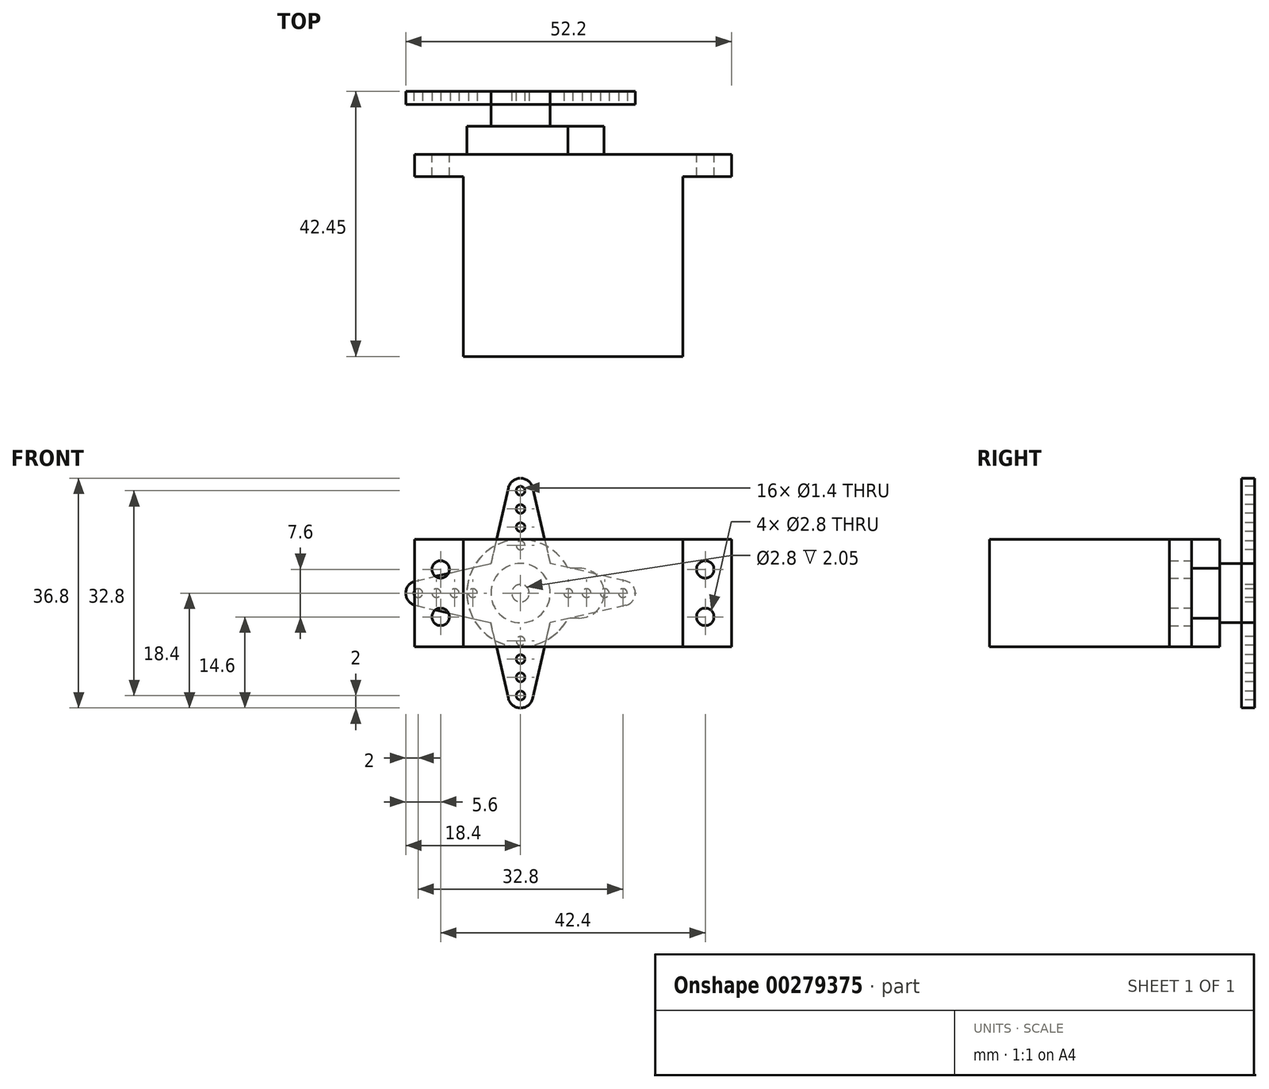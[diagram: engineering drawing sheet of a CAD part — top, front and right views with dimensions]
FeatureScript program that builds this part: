
annotation { "Feature Type Name" : "Feature", "Feature Type Description" : "" }
export const myFeature = defineFeature(function(context is Context, id is Id, definition is map)
    precondition{}
    {
        {
            var Q0;
            Q0=qCreatedBy(makeId("Top.planeOp"),FACE);
            var sketch = newSketch(context, id + "F0", { "sketchPlane" : qUnion([Q0])});
            skLineSegment(sketch, "E0.bottom", {"start": v(17.6, -16.2) * mm, "end": v(-17.6, -16.2) * mm});
            skLineSegment(sketch, "E0.top", {"start": v(17.6, 16.2) * mm, "end": v(-17.6, 16.2) * mm});
            skLineSegment(sketch, "E0.left", {"start": v(17.6, -16.2) * mm, "end": v(17.6, 12.6) * mm});
            skLineSegment(sketch, "E0.right", {"start": v(-17.6, -16.2) * mm, "end": v(-17.6, 12.6) * mm});
            skPoint(sketch, "E0.middle", {"position": v(0, 0) * mm});
            skLineSegment(sketch, "E1.bottom", {"start": v(17.6, 16.2) * mm, "end": v(25.4, 16.2) * mm});
            skLineSegment(sketch, "E1.top", {"start": v(17.6, 12.6) * mm, "end": v(25.4, 12.6) * mm});
            skLineSegment(sketch, "E1.right", {"start": v(25.4, 16.2) * mm, "end": v(25.4, 12.6) * mm});
            skLineSegment(sketch, "E2.MirrorCS", {"start": v(-17.6, 16.2) * mm, "end": v(-25.4, 16.2) * mm});
            skLineSegment(sketch, "E3.MirrorCS", {"start": v(-25.4, 16.2) * mm, "end": v(-25.4, 12.6) * mm});
            skLineSegment(sketch, "E4.MirrorCS", {"start": v(-17.6, 12.6) * mm, "end": v(-25.4, 12.6) * mm});
            skSolve(sketch);
        }
        {
            var Q0;
            Q0=makeQuery(id+"F0.imprint","IMPRINT",FACE,{"disambiguationData":[TD([[makeQuery(id+"F0.imprint","IMPRINT",EDGE,{"derivedFrom":sQuery(id+"F0.wireOp",EDGE,"E0.bottom")}),-1.0]])]});
            extrude(context, id + "F1", {"entities" : qUnion([Q0]), "endBound" : BoundingType.SYMMETRIC, "depth" : 17.2 * mm});
        }
        {
            var Q0;
            Q0=makeQuery(id+"F1.opExtrude","SWEPT_FACE",FACE,{"disambiguationData":[OSD([sQuery(id+"F0.wireOp",EDGE,"E0.top"),sQuery(id+"F0.wireOp",EDGE,"E1.bottom"),sQuery(id+"F0.wireOp",EDGE,"E2.MirrorCS")])]});
            var sketch = newSketch(context, id + "F2", { "sketchPlane" : qUnion([Q0])});
            skArc(sketch, "E5", {"start": v(0.79, -4) * mm, "mid": v(17, 0) * mm, "end": v(0.79, 4) * mm});
            skArc(sketch, "E6", {"start": v(-1, 4) * mm, "mid": v(-5, 0) * mm, "end": v(-1, -4) * mm});
            skLineSegment(sketch, "E7", {"start": v(-1, -4) * mm, "end": v(0.79, -4) * mm});
            skLineSegment(sketch, "E8", {"start": v(-1, 4) * mm, "end": v(0.79, 4) * mm});
            skCircle(sketch, "E9", {"center": v(8.4, 0) * mm, "radius": 2.95 * mm});
            skSolve(sketch);
        }
        {
            var Q0;
            Q0=makeQuery(id+"F2.imprint","IMPRINT",FACE,{"disambiguationData":[TD([[makeQuery(id+"F2.imprint","IMPRINT",EDGE,{"derivedFrom":sQuery(id+"F2.wireOp",EDGE,"E6")}),1.0]])]});
            extrude(context, id + "F3", {"entities" : qUnion([Q0]), "operationType" : NewBodyOperationType.ADD, "depth" : 4.5 * mm});
        }
        {
            var Q0;
            Q0=makeQuery(id+"F2.imprint","IMPRINT",FACE,{"disambiguationData":[TD([[makeQuery(id+"F2.imprint","IMPRINT",EDGE,{"derivedFrom":sQuery(id+"F2.wireOp",EDGE,"E9")}),1.0]])]});
            extrude(context, id + "F4", {"entities" : qUnion([Q0]), "operationType" : NewBodyOperationType.ADD, "depth" : 8 * mm});
        }
        {
            var Q0;
            {var subQ0=sQuery(id+"F0.wireOp",EDGE,"E2.MirrorCS");var subQ1=sQuery(id+"F0.wireOp",EDGE,"E1.bottom");var subQ2=sQuery(id+"F0.wireOp",EDGE,"E0.top");var subQ3=makeQuery(id+"F1.opExtrude","SWEPT_FACE",FACE,{"disambiguationData":[OSD([subQ2,subQ1,subQ0])]});var subQ4=sQuery(id+"F0.wireOp",EDGE,"E1.right");Q0=makeQuery(id+"F3.boolean.opBoolean","SPLIT",FACE,{"disambiguationData":[TD([makeQuery(id+"F1.opExtrude","SWEPT_FACE",FACE,{"disambiguationData":[OSD([subQ4])]})])],"derivedFrom":subQ3});}
            var sketch = newSketch(context, id + "F5", { "sketchPlane" : qUnion([Q0])});
            skCircle(sketch, "E10", {"center": v(-21.2, 3.8) * mm, "radius": 1.4 * mm});
            skCircle(sketch, "E11.MirrorC", {"center": v(-21.2, -3.8) * mm, "radius": 1.4 * mm});
            skCircle(sketch, "E12.MirrorC", {"center": v(21.2, 3.8) * mm, "radius": 1.4 * mm});
            skCircle(sketch, "E13.MirrorC", {"center": v(21.2, -3.8) * mm, "radius": 1.4 * mm});
            skSolve(sketch);
        }
        {
            var Q0;
            Q0 = qSketchRegion(id + "F5", true);
            extrude(context, id + "F6", {"entities" : qUnion([Q0]), "operationType" : NewBodyOperationType.REMOVE, "endBound" : BoundingType.UP_TO_NEXT, "oppositeDirection" : true, "depth" : 25 * mm});
        }
        {
            var Q0;
            Q0=makeQuery(id+"F4.opExtrude","CAP_FACE",FACE,{"disambiguationData":[OSD([sQuery(id+"F2.wireOp",EDGE,"E9")])],"isStart":false});
            var sketch = newSketch(context, id + "F7", { "sketchPlane" : qUnion([Q0])});
            skCircle(sketch, "E14.0", {"center": v(8.4, 0) * mm, "radius": 2.95 * mm});
            skCircle(sketch, "E15", {"center": v(8.4, 0) * mm, "radius": 4.75 * mm});
            skArc(sketch, "E16", {"start": v(25.25, -1.95) * mm, "mid": v(26.8, 0) * mm, "end": v(25.25, 1.95) * mm});
            skLineSegment(sketch, "E17", {"start": v(25.25, 1.95) * mm, "end": v(13.15, 4.75) * mm});
            skLineSegment(sketch, "E18", {"start": v(25.25, -1.95) * mm, "end": v(13.15, -4.75) * mm});
            skLineSegment(sketch, "E19.1.0", {"start": v(10.35, 16.85) * mm, "end": v(13.15, 4.75) * mm});
            skLineSegment(sketch, "E19.1.1", {"start": v(6.45, 16.85) * mm, "end": v(3.65, 4.75) * mm});
            skArc(sketch, "E19.1.2", {"start": v(10.35, 16.85) * mm, "mid": v(8.4, 18.4) * mm, "end": v(6.45, 16.85) * mm});
            skLineSegment(sketch, "E19.2.0", {"start": v(-8.45, 1.95) * mm, "end": v(3.65, 4.75) * mm});
            skLineSegment(sketch, "E19.2.1", {"start": v(-8.45, -1.95) * mm, "end": v(3.65, -4.75) * mm});
            skArc(sketch, "E19.2.2", {"start": v(-8.45, 1.95) * mm, "mid": v(-10, 0) * mm, "end": v(-8.45, -1.95) * mm});
            skLineSegment(sketch, "E19.3.0", {"start": v(6.45, -16.85) * mm, "end": v(3.65, -4.75) * mm});
            skLineSegment(sketch, "E19.3.1", {"start": v(10.35, -16.85) * mm, "end": v(13.15, -4.75) * mm});
            skArc(sketch, "E19.3.2", {"start": v(6.45, -16.85) * mm, "mid": v(8.4, -18.4) * mm, "end": v(10.35, -16.85) * mm});
            skCircle(sketch, "E20", {"center": v(24.8, 0) * mm, "radius": 0.7 * mm});
            skCircle(sketch, "E21.1.0.0", {"center": v(21.88, 0) * mm, "radius": 0.7 * mm});
            skCircle(sketch, "E21.2.0.0", {"center": v(18.97, 0) * mm, "radius": 0.7 * mm});
            skCircle(sketch, "E21.3.0.0", {"center": v(16.05, 0) * mm, "radius": 0.7 * mm});
            skLineSegment(sketch, "E21.direction1", {"start": v(24.8, 0) * mm, "end": v(21.88, 0) * mm, "construction": true});
            skCircle(sketch, "E22.1.0", {"center": v(8.4, 7.65) * mm, "radius": 0.7 * mm});
            skCircle(sketch, "E22.1.1", {"center": v(8.4, 16.4) * mm, "radius": 0.7 * mm});
            skCircle(sketch, "E22.1.2", {"center": v(8.4, 13.48) * mm, "radius": 0.7 * mm});
            skCircle(sketch, "E22.1.3", {"center": v(8.4, 10.57) * mm, "radius": 0.7 * mm});
            skLineSegment(sketch, "E22.1.4", {"start": v(8.4, 16.4) * mm, "end": v(8.4, 13.48) * mm, "construction": true});
            skCircle(sketch, "E22.2.0", {"center": v(0.75, 0) * mm, "radius": 0.7 * mm});
            skCircle(sketch, "E22.2.1", {"center": v(-8, 0) * mm, "radius": 0.7 * mm});
            skCircle(sketch, "E22.2.2", {"center": v(-5.08, 0) * mm, "radius": 0.7 * mm});
            skCircle(sketch, "E22.2.3", {"center": v(-2.17, 0) * mm, "radius": 0.7 * mm});
            skLineSegment(sketch, "E22.2.4", {"start": v(-8, 0) * mm, "end": v(-5.08, 0) * mm, "construction": true});
            skCircle(sketch, "E22.3.0", {"center": v(8.4, -7.65) * mm, "radius": 0.7 * mm});
            skCircle(sketch, "E22.3.1", {"center": v(8.4, -16.4) * mm, "radius": 0.7 * mm});
            skCircle(sketch, "E22.3.2", {"center": v(8.4, -13.48) * mm, "radius": 0.7 * mm});
            skCircle(sketch, "E22.3.3", {"center": v(8.4, -10.57) * mm, "radius": 0.7 * mm});
            skLineSegment(sketch, "E22.3.4", {"start": v(8.4, -16.4) * mm, "end": v(8.4, -13.48) * mm, "construction": true});
            skCircle(sketch, "E23", {"center": v(8.4, 0) * mm, "radius": 1.4 * mm});
            skSolve(sketch);
        }
        {
            var Q0;
            Q0=makeQuery(id+"F7.imprint","IMPRINT",FACE,{"disambiguationData":[TD([[makeQuery(id+"F7.imprint","IMPRINT",EDGE,{"derivedFrom":sQuery(id+"F7.wireOp",EDGE,"E15")}),-1.0]])]});
            var Q1;
            Q1=makeQuery(id+"F7.imprint","IMPRINT",FACE,{"disambiguationData":[TD([[makeQuery(id+"F7.imprint","IMPRINT",EDGE,{"derivedFrom":sQuery(id+"F7.wireOp",EDGE,"E14.0")}),-1.0]])]});
            var Q2;
            Q2=makeQuery(id+"F7.imprint","IMPRINT",FACE,{"disambiguationData":[TD([[makeQuery(id+"F7.imprint","IMPRINT",EDGE,{"derivedFrom":sQuery(id+"F7.wireOp",EDGE,"E14.0")}),1.0]])]});
            extrude(context, id + "F8", {"entities" : qUnion([Q0, Q1, Q2]), "depth" : 2.05 * mm});
        }
        {
            var Q0;
            Q0=makeQuery(id+"F7.imprint","IMPRINT",FACE,{"disambiguationData":[TD([[makeQuery(id+"F7.imprint","IMPRINT",EDGE,{"derivedFrom":sQuery(id+"F7.wireOp",EDGE,"E14.0")}),-1.0]])]});
            extrude(context, id + "F9", {"entities" : qUnion([Q0]), "operationType" : NewBodyOperationType.ADD, "oppositeDirection" : true, "depth" : 3.5 * mm});
        }
    });
